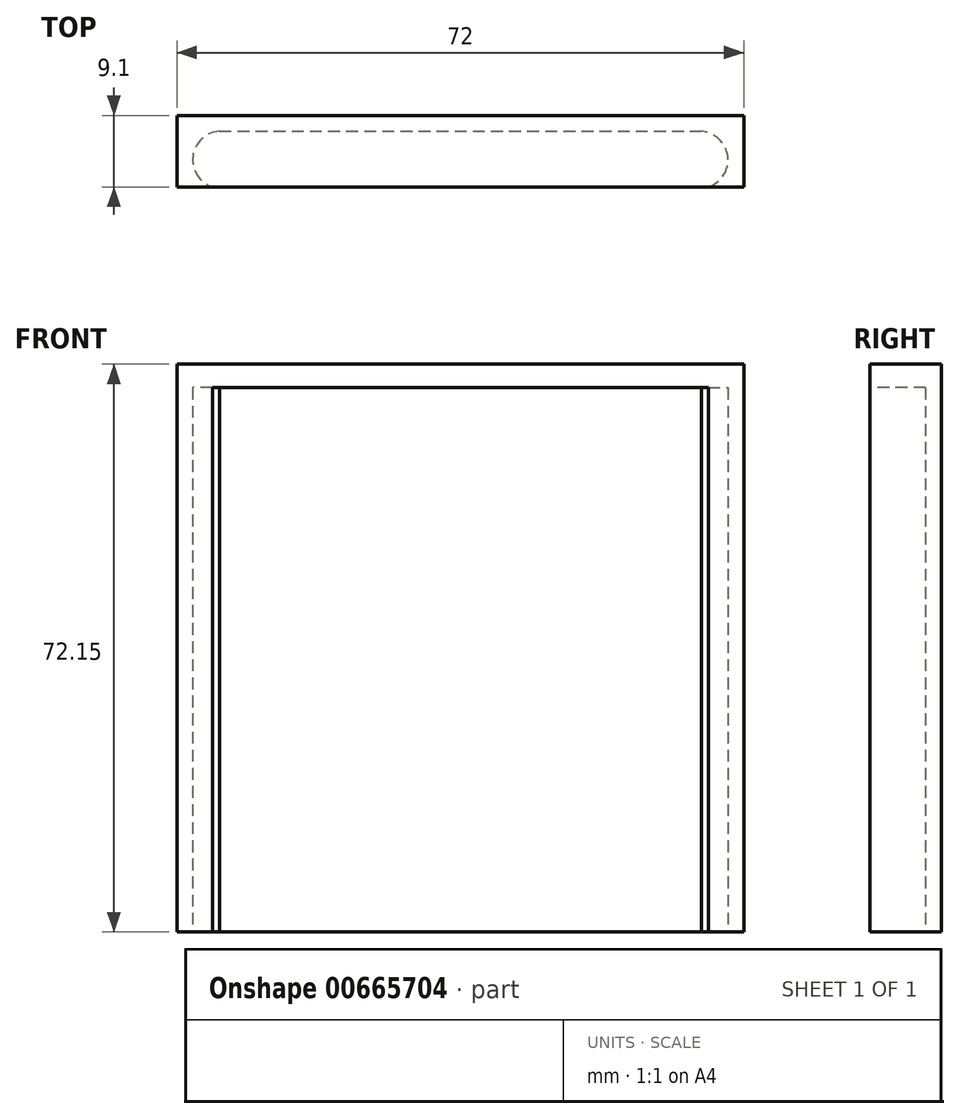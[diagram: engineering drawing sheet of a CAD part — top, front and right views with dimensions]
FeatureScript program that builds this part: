
annotation { "Feature Type Name" : "Feature", "Feature Type Description" : "" }
export const myFeature = defineFeature(function(context is Context, id is Id, definition is map)
    precondition{}
    {
        {
            var Q0;
            Q0=qCreatedBy(makeId("Top.planeOp"),FACE);
            var sketch = newSketch(context, id + "F0", { "sketchPlane" : qUnion([Q0])});
            skLineSegment(sketch, "E0.bottom", {"start": v(-36, 4.55) * mm, "end": v(36, 4.55) * mm});
            skLineSegment(sketch, "E0.top", {"start": v(-36, -4.55) * mm, "end": v(36, -4.55) * mm});
            skLineSegment(sketch, "E0.left", {"start": v(-36, 4.55) * mm, "end": v(-36, -4.55) * mm});
            skLineSegment(sketch, "E0.right", {"start": v(36, 4.55) * mm, "end": v(36, -4.55) * mm});
            skPoint(sketch, "E0.middle", {"position": v(0, 0) * mm});
            skLineSegment(sketch, "E1.bottom", {"start": v(-34, -4.55) * mm, "end": v(34, -4.55) * mm});
            skLineSegment(sketch, "E1.top", {"start": v(-34, 2.55) * mm, "end": v(34, 2.55) * mm});
            skLineSegment(sketch, "E1.left", {"start": v(-34, -4.55) * mm, "end": v(-34, 2.55) * mm});
            skLineSegment(sketch, "E1.right", {"start": v(34, -4.55) * mm, "end": v(34, 2.55) * mm});
            skArc(sketch, "E2", {"start": v(31.5, -4.55) * mm, "mid": v(33.97, -0.63) * mm, "end": v(30.6, 2.55) * mm});
            skArc(sketch, "E3", {"start": v(-30.6, 2.55) * mm, "mid": v(-33.97, -0.63) * mm, "end": v(-31.5, -4.55) * mm});
            skSolve(sketch);
        }
        {
            var Q0;
            Q0=makeQuery(id+"F0.imprint","IMPRINT",FACE,{"disambiguationData":[TD([[makeQuery(id+"F0.imprint","IMPRINT",EDGE,{"derivedFrom":sQuery(id+"F0.wireOp",EDGE,"E0.bottom")}),-1.0]])]});
            var Q1;
            {var subQ0=sQuery(id+"F0.wireOp",EDGE,"E3");var subQ1=sQuery(id+"F0.wireOp",EDGE,"E1.top");var subQ2=makeQuery(id+"F0.imprint","INTERSECT",VERTEX,{"derivedFrom":[subQ1,subQ0]});Q1=makeQuery(id+"F0.imprint","IMPRINT",FACE,{"disambiguationData":[TD([[makeQuery(id+"F0.imprint","IMPRINT",EDGE,{"disambiguationData":[TD([[subQ2,1.0]])],"derivedFrom":subQ1}),-1.0]])]});}
            var Q2;
            {var subQ0=sQuery(id+"F0.wireOp",EDGE,"E3");var subQ1=sQuery(id+"F0.wireOp",EDGE,"E0.top");var subQ2=makeQuery(id+"F0.imprint","INTERSECT",VERTEX,{"derivedFrom":[subQ1,subQ0]});Q2=makeQuery(id+"F0.imprint","IMPRINT",FACE,{"disambiguationData":[TD([[makeQuery(id+"F0.imprint","IMPRINT",EDGE,{"disambiguationData":[TD([[subQ2,1.0]])],"derivedFrom":subQ1}),1.0]])]});}
            var Q3;
            {var subQ0=sQuery(id+"F0.wireOp",EDGE,"E1.right");var subQ1=sQuery(id+"F0.wireOp",EDGE,"E1.top");var subQ2=makeQuery(id+"F0.imprint","INTERSECT",VERTEX,{"derivedFrom":[subQ1,subQ0]});Q3=makeQuery(id+"F0.imprint","IMPRINT",FACE,{"disambiguationData":[TD([[makeQuery(id+"F0.imprint","IMPRINT",EDGE,{"disambiguationData":[TD([[subQ2,1.0]])],"derivedFrom":subQ1}),-1.0]])]});}
            var Q4;
            {var subQ0=sQuery(id+"F0.wireOp",EDGE,"E2");var subQ1=sQuery(id+"F0.wireOp",EDGE,"E0.top");var subQ2=makeQuery(id+"F0.imprint","INTERSECT",VERTEX,{"derivedFrom":[subQ1,subQ0]});Q4=makeQuery(id+"F0.imprint","IMPRINT",FACE,{"disambiguationData":[TD([[makeQuery(id+"F0.imprint","IMPRINT",EDGE,{"disambiguationData":[TD([[subQ2,-1.0]])],"derivedFrom":subQ1}),1.0]])]});}
            extrude(context, id + "F1", {"entities" : qUnion([Q0, Q1, Q2, Q3, Q4]), "depth" : 69.15 * mm, "offsetDistance" : 25 * mm});
        }
        {
            var Q0;
            Q0=makeQuery(id+"F1.opExtrude","CAP_FACE",FACE,{"disambiguationData":[OSD([sQuery(id+"F0.wireOp",EDGE,"E0.bottom"),sQuery(id+"F0.wireOp",EDGE,"E0.top"),sQuery(id+"F0.wireOp",EDGE,"E0.left"),sQuery(id+"F0.wireOp",EDGE,"E0.right"),sQuery(id+"F0.wireOp",EDGE,"E1.top"),sQuery(id+"F0.wireOp",EDGE,"E2"),sQuery(id+"F0.wireOp",EDGE,"E3")])],"isStart":false});
            var sketch = newSketch(context, id + "F2", { "sketchPlane" : qUnion([Q0])});
            skLineSegment(sketch, "E4.bottom", {"start": v(-36, 4.55) * mm, "end": v(36, 4.55) * mm});
            skLineSegment(sketch, "E4.top", {"start": v(-36, -4.55) * mm, "end": v(36, -4.55) * mm});
            skLineSegment(sketch, "E4.left", {"start": v(-36, 4.55) * mm, "end": v(-36, -4.55) * mm});
            skLineSegment(sketch, "E4.right", {"start": v(36, 4.55) * mm, "end": v(36, -4.55) * mm});
            skSolve(sketch);
        }
        {
            var Q0;
            Q0=makeQuery(id+"F2.imprint","IMPRINT",FACE,{"disambiguationData":[TD([[makeQuery(id+"F2.imprint","IMPRINT",EDGE,{"derivedFrom":makeQuery(id+"F1.opExtrude","CAP_EDGE",EDGE,{"disambiguationData":[OSD([sQuery(id+"F0.wireOp",EDGE,"E1.top")])],"isStart":false})}),-1.0]])]});
            var Q1;
            Q1=makeQuery(id+"F2.imprint","IMPRINT",FACE,{"disambiguationData":[TD([[makeQuery(id+"F2.imprint","IMPRINT",EDGE,{"derivedFrom":sQuery(id+"F2.wireOp",EDGE,"E4.bottom")}),-1.0]])]});
            extrude(context, id + "F3", {"entities" : qUnion([Q0, Q1]), "operationType" : NewBodyOperationType.ADD, "depth" : 3 * mm, "offsetDistance" : 25 * mm});
        }
    });
